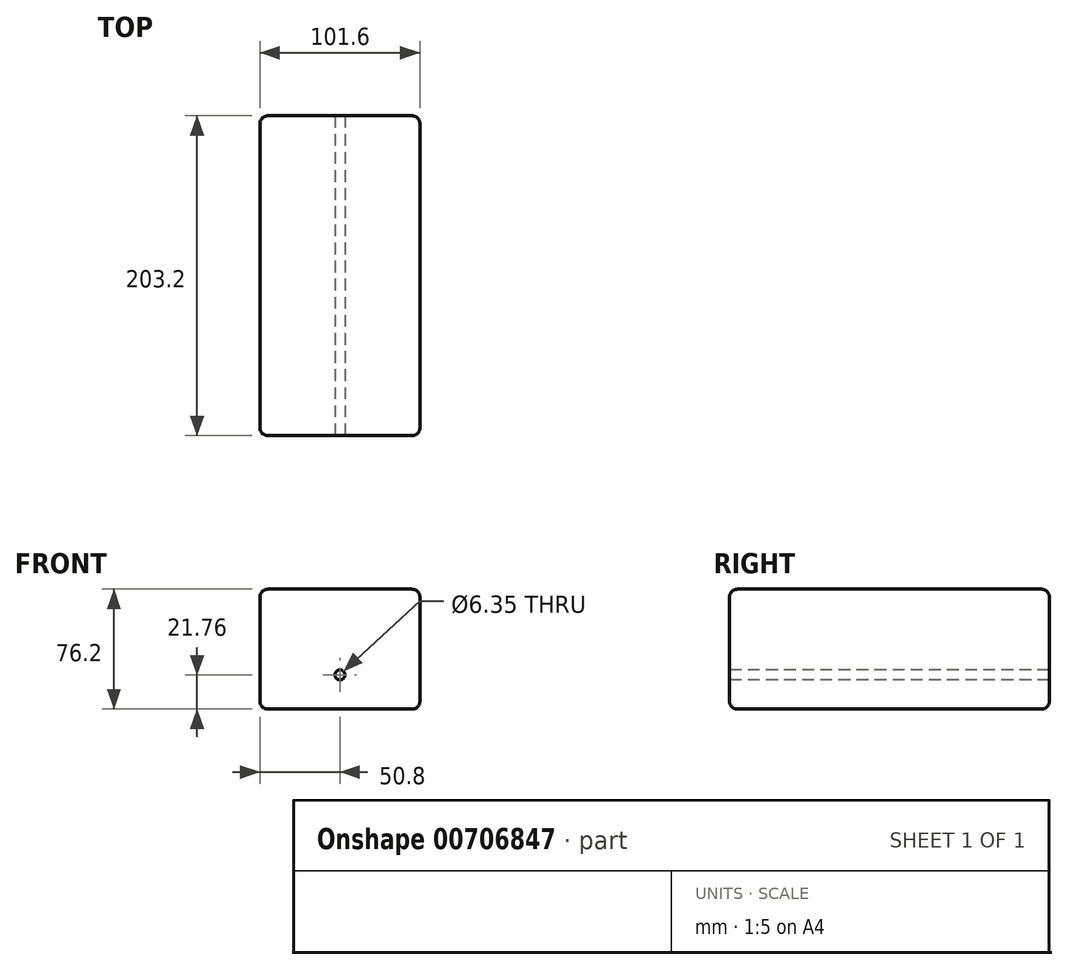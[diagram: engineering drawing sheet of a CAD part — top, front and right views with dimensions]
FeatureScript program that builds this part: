
annotation { "Feature Type Name" : "Feature", "Feature Type Description" : "" }
export const myFeature = defineFeature(function(context is Context, id is Id, definition is map)
    precondition{}
    {
        {
            var Q0;
            Q0=qCreatedBy(makeId("Front.planeOp"),FACE);
            var sketch = newSketch(context, id + "F0", { "sketchPlane" : qUnion([Q0])});
            skLineSegment(sketch, "E0.bottom", {"start": v(-50.8, -38.1) * mm, "end": v(50.8, -38.1) * mm});
            skLineSegment(sketch, "E0.top", {"start": v(-50.8, 38.1) * mm, "end": v(50.8, 38.1) * mm});
            skLineSegment(sketch, "E0.left", {"start": v(-50.8, -38.1) * mm, "end": v(-50.8, 38.1) * mm});
            skLineSegment(sketch, "E0.right", {"start": v(50.8, -38.1) * mm, "end": v(50.8, 38.1) * mm});
            skPoint(sketch, "E0.middle", {"position": v(0, 0) * mm});
            skSolve(sketch);
        }
        {
            var Q0;
            Q0=qSketchRegion(id+"F0",true);
            extrude(context, id + "F1", {"entities" : qUnion([Q0]), "endBound" : BoundingType.SYMMETRIC, "depth" : 203.2 * mm, "offsetDistance" : 25.4 * mm});
        }
        {
            var Q0;
            Q0=makeQuery(id+"F1.opExtrude","CAP_EDGE",EDGE,{"disambiguationData":[OSD([sQuery(id+"F0.wireOp",EDGE,"E0.top")])],"isStart":false});
            var Q1;
            Q1=makeQuery(id+"F1.opExtrude","SWEPT_EDGE",EDGE,{"disambiguationData":[OSD([sQuery(id+"F0.wireOp",EDGE,"E0.top"),sQuery(id+"F0.wireOp",EDGE,"E0.right")])]});
            var Q2;
            Q2=makeQuery(id+"F1.opExtrude","SWEPT_EDGE",EDGE,{"disambiguationData":[OSD([sQuery(id+"F0.wireOp",EDGE,"E0.top"),sQuery(id+"F0.wireOp",EDGE,"E0.left")])]});
            var Q3;
            Q3=makeQuery(id+"F1.opExtrude","CAP_EDGE",EDGE,{"disambiguationData":[OSD([sQuery(id+"F0.wireOp",EDGE,"E0.left")])],"isStart":false});
            var Q4;
            Q4=makeQuery(id+"F1.opExtrude","CAP_EDGE",EDGE,{"disambiguationData":[OSD([sQuery(id+"F0.wireOp",EDGE,"E0.right")])],"isStart":false});
            var Q5;
            Q5=makeQuery(id+"F1.opExtrude","CAP_FACE",FACE,{"disambiguationData":[OSD([sQuery(id+"F0.wireOp",EDGE,"E0.bottom"),sQuery(id+"F0.wireOp",EDGE,"E0.top"),sQuery(id+"F0.wireOp",EDGE,"E0.left"),sQuery(id+"F0.wireOp",EDGE,"E0.right")])],"isStart":true});
            var Q6;
            Q6=makeQuery(id+"F1.opExtrude","SWEPT_FACE",FACE,{"disambiguationData":[OSD([sQuery(id+"F0.wireOp",EDGE,"E0.right")])]});
            var Q7;
            Q7=makeQuery(id+"F1.opExtrude","SWEPT_EDGE",EDGE,{"disambiguationData":[OSD([sQuery(id+"F0.wireOp",EDGE,"E0.bottom"),sQuery(id+"F0.wireOp",EDGE,"E0.right")])]});
            var Q8;
            Q8=makeQuery(id+"F1.opExtrude","SWEPT_EDGE",EDGE,{"disambiguationData":[OSD([sQuery(id+"F0.wireOp",EDGE,"E0.bottom"),sQuery(id+"F0.wireOp",EDGE,"E0.left")])]});
            fillet(context, id + "F2", {"entities" : qUnion([Q0, Q1, Q2, Q3, Q4, Q5, Q6, Q7, Q8]), "radius" : 5.08 * mm, "tangentPropagation" : true, "allowEdgeOverflow" : false});
        }
        {
            var Q0;
            Q0=makeQuery(id+"FGfTKkmkADLqAxq_1.opShell","OFFSET_EDGE",EDGE,{"disambiguationData":[OSD([sQuery(id+"F0.wireOp",EDGE,"E0.top"),sQuery(id+"F0.wireOp",EDGE,"E0.right")])]});
            var Q1;
            {var subQ0=sQuery(id+"F0.wireOp",EDGE,"E0.top");var subQ1=makeQuery(id+"F1.opExtrude","CAP_EDGE",EDGE,{"disambiguationData":[OSD([subQ0])],"isStart":true});var subQ2=sQuery(id+"F0.wireOp",EDGE,"E0.right");var subQ3=sQuery(id+"F0.wireOp",EDGE,"E0.left");var subQ4=sQuery(id+"F0.wireOp",EDGE,"E0.bottom");Q1=makeQuery(id+"FGfTKkmkADLqAxq_1.opShell","OFFSET_EDGE",EDGE,{"disambiguationData":[OSD([subQ4,subQ0,subQ3,subQ2]),TDD([makeQuery(id+"F2.opFillet","BLEND_EDGE",EDGE,{"blendedFrom":[subQ1,makeQuery(id+"F1.opExtrude","CAP_FACE",FACE,{"disambiguationData":[OSD([subQ4,subQ0,subQ3,subQ2])],"isStart":true})],"blendedInto":[makeQuery(id+"F1.opExtrude","CAP_FACE",FACE,{"disambiguationData":[OSD([subQ4,subQ0,subQ3,subQ2])],"isStart":true})]}),makeQuery(id+"F2.opFillet","BLEND_EDGE",EDGE,{"blendedFrom":[subQ1,makeQuery(id+"F1.opExtrude","SWEPT_FACE",FACE,{"disambiguationData":[OSD([subQ0])]})],"blendedInto":[makeQuery(id+"F1.opExtrude","SWEPT_FACE",FACE,{"disambiguationData":[OSD([subQ0])]})]})])]});}
            var Q2;
            {var subQ0=sQuery(id+"F0.wireOp",EDGE,"E0.left");var subQ1=makeQuery(id+"F1.opExtrude","CAP_EDGE",EDGE,{"disambiguationData":[OSD([subQ0])],"isStart":true});var subQ2=sQuery(id+"F0.wireOp",EDGE,"E0.right");var subQ3=sQuery(id+"F0.wireOp",EDGE,"E0.top");var subQ4=sQuery(id+"F0.wireOp",EDGE,"E0.bottom");Q2=makeQuery(id+"FGfTKkmkADLqAxq_1.opShell","OFFSET_EDGE",EDGE,{"disambiguationData":[OSD([subQ4,subQ3,subQ0,subQ2]),TDD([makeQuery(id+"F2.opFillet","BLEND_EDGE",EDGE,{"blendedFrom":[subQ1,makeQuery(id+"F1.opExtrude","CAP_FACE",FACE,{"disambiguationData":[OSD([subQ4,subQ3,subQ0,subQ2])],"isStart":true})],"blendedInto":[makeQuery(id+"F1.opExtrude","CAP_FACE",FACE,{"disambiguationData":[OSD([subQ4,subQ3,subQ0,subQ2])],"isStart":true})]}),makeQuery(id+"F2.opFillet","BLEND_EDGE",EDGE,{"blendedFrom":[subQ1,makeQuery(id+"F1.opExtrude","SWEPT_FACE",FACE,{"disambiguationData":[OSD([subQ0])]})],"blendedInto":[makeQuery(id+"F1.opExtrude","SWEPT_FACE",FACE,{"disambiguationData":[OSD([subQ0])]})]})])]});}
            var Q3;
            {var subQ0=sQuery(id+"F0.wireOp",EDGE,"E0.right");var subQ1=makeQuery(id+"F1.opExtrude","CAP_EDGE",EDGE,{"disambiguationData":[OSD([subQ0])],"isStart":true});var subQ2=sQuery(id+"F0.wireOp",EDGE,"E0.left");var subQ3=sQuery(id+"F0.wireOp",EDGE,"E0.top");var subQ4=sQuery(id+"F0.wireOp",EDGE,"E0.bottom");Q3=makeQuery(id+"FGfTKkmkADLqAxq_1.opShell","OFFSET_EDGE",EDGE,{"disambiguationData":[OSD([subQ4,subQ3,subQ2,subQ0]),TDD([makeQuery(id+"F2.opFillet","BLEND_EDGE",EDGE,{"blendedFrom":[subQ1,makeQuery(id+"F1.opExtrude","CAP_FACE",FACE,{"disambiguationData":[OSD([subQ4,subQ3,subQ2,subQ0])],"isStart":true})],"blendedInto":[makeQuery(id+"F1.opExtrude","CAP_FACE",FACE,{"disambiguationData":[OSD([subQ4,subQ3,subQ2,subQ0])],"isStart":true})]}),makeQuery(id+"F2.opFillet","BLEND_EDGE",EDGE,{"blendedFrom":[subQ1,makeQuery(id+"F1.opExtrude","SWEPT_FACE",FACE,{"disambiguationData":[OSD([subQ0])]})],"blendedInto":[makeQuery(id+"F1.opExtrude","SWEPT_FACE",FACE,{"disambiguationData":[OSD([subQ0])]})]})])]});}
            var Q4;
            Q4=makeQuery(id+"FGfTKkmkADLqAxq_1.opShell","OFFSET_EDGE",EDGE,{"disambiguationData":[OSD([sQuery(id+"F0.wireOp",EDGE,"E0.top"),sQuery(id+"F0.wireOp",EDGE,"E0.left")])]});
            var Q5;
            {var subQ0=sQuery(id+"F0.wireOp",EDGE,"E0.right");var subQ1=sQuery(id+"F0.wireOp",EDGE,"E0.left");var subQ2=sQuery(id+"F0.wireOp",EDGE,"E0.top");var subQ3=sQuery(id+"F0.wireOp",EDGE,"E0.bottom");var subQ4=makeQuery(id+"F1.opExtrude","CAP_EDGE",EDGE,{"disambiguationData":[OSD([subQ3])],"isStart":true});Q5=makeQuery(id+"FGfTKkmkADLqAxq_1.opShell","OFFSET_EDGE",EDGE,{"disambiguationData":[OSD([subQ3,subQ2,subQ1,subQ0]),TDD([makeQuery(id+"F2.opFillet","BLEND_EDGE",EDGE,{"blendedFrom":[subQ4,makeQuery(id+"F1.opExtrude","SWEPT_FACE",FACE,{"disambiguationData":[OSD([subQ3])]})],"blendedInto":[makeQuery(id+"F1.opExtrude","SWEPT_FACE",FACE,{"disambiguationData":[OSD([subQ3])]})]}),makeQuery(id+"F2.opFillet","BLEND_EDGE",EDGE,{"blendedFrom":[subQ4,makeQuery(id+"F1.opExtrude","CAP_FACE",FACE,{"disambiguationData":[OSD([subQ3,subQ2,subQ1,subQ0])],"isStart":true})],"blendedInto":[makeQuery(id+"F1.opExtrude","CAP_FACE",FACE,{"disambiguationData":[OSD([subQ3,subQ2,subQ1,subQ0])],"isStart":true})]})])]});}
            var Q6;
            Q6=makeQuery(id+"FGfTKkmkADLqAxq_1.opShell","OFFSET_EDGE",EDGE,{"disambiguationData":[OSD([sQuery(id+"F0.wireOp",EDGE,"E0.bottom"),sQuery(id+"F0.wireOp",EDGE,"E0.left")])]});
            var Q7;
            Q7=makeQuery(id+"FGfTKkmkADLqAxq_1.opShell","OFFSET_EDGE",EDGE,{"disambiguationData":[OSD([sQuery(id+"F0.wireOp",EDGE,"E0.bottom")])]});
            var Q8;
            {var subQ0=sQuery(id+"F0.wireOp",EDGE,"E0.left");var subQ1=makeQuery(id+"F1.opExtrude","CAP_EDGE",EDGE,{"disambiguationData":[OSD([subQ0])],"isStart":false});var subQ2=sQuery(id+"F0.wireOp",EDGE,"E0.right");var subQ3=sQuery(id+"F0.wireOp",EDGE,"E0.top");var subQ4=sQuery(id+"F0.wireOp",EDGE,"E0.bottom");Q8=makeQuery(id+"FGfTKkmkADLqAxq_1.opShell","OFFSET_EDGE",EDGE,{"disambiguationData":[OSD([subQ4,subQ3,subQ0,subQ2]),TDD([makeQuery(id+"F2.opFillet","BLEND_EDGE",EDGE,{"blendedFrom":[subQ1,makeQuery(id+"F1.opExtrude","CAP_FACE",FACE,{"disambiguationData":[OSD([subQ4,subQ3,subQ0,subQ2])],"isStart":false})],"blendedInto":[makeQuery(id+"F1.opExtrude","CAP_FACE",FACE,{"disambiguationData":[OSD([subQ4,subQ3,subQ0,subQ2])],"isStart":false})]}),makeQuery(id+"F2.opFillet","BLEND_EDGE",EDGE,{"blendedFrom":[subQ1,makeQuery(id+"F1.opExtrude","SWEPT_FACE",FACE,{"disambiguationData":[OSD([subQ0])]})],"blendedInto":[makeQuery(id+"F1.opExtrude","SWEPT_FACE",FACE,{"disambiguationData":[OSD([subQ0])]})]})])]});}
            var Q9;
            {var subQ0=sQuery(id+"F0.wireOp",EDGE,"E0.top");var subQ1=makeQuery(id+"F1.opExtrude","CAP_EDGE",EDGE,{"disambiguationData":[OSD([subQ0])],"isStart":false});var subQ2=sQuery(id+"F0.wireOp",EDGE,"E0.right");var subQ3=sQuery(id+"F0.wireOp",EDGE,"E0.left");var subQ4=sQuery(id+"F0.wireOp",EDGE,"E0.bottom");Q9=makeQuery(id+"FGfTKkmkADLqAxq_1.opShell","OFFSET_EDGE",EDGE,{"disambiguationData":[OSD([subQ4,subQ0,subQ3,subQ2]),TDD([makeQuery(id+"F2.opFillet","BLEND_EDGE",EDGE,{"blendedFrom":[subQ1,makeQuery(id+"F1.opExtrude","CAP_FACE",FACE,{"disambiguationData":[OSD([subQ4,subQ0,subQ3,subQ2])],"isStart":false})],"blendedInto":[makeQuery(id+"F1.opExtrude","CAP_FACE",FACE,{"disambiguationData":[OSD([subQ4,subQ0,subQ3,subQ2])],"isStart":false})]}),makeQuery(id+"F2.opFillet","BLEND_EDGE",EDGE,{"blendedFrom":[subQ1,makeQuery(id+"F1.opExtrude","SWEPT_FACE",FACE,{"disambiguationData":[OSD([subQ0])]})],"blendedInto":[makeQuery(id+"F1.opExtrude","SWEPT_FACE",FACE,{"disambiguationData":[OSD([subQ0])]})]})])]});}
            var Q10;
            Q10=makeQuery(id+"FGfTKkmkADLqAxq_1.opShell","OFFSET_EDGE",EDGE,{"disambiguationData":[OSD([sQuery(id+"F0.wireOp",EDGE,"E0.bottom"),sQuery(id+"F0.wireOp",EDGE,"E0.right")])]});
            var Q11;
            {var subQ0=sQuery(id+"F0.wireOp",EDGE,"E0.right");var subQ1=makeQuery(id+"F1.opExtrude","CAP_EDGE",EDGE,{"disambiguationData":[OSD([subQ0])],"isStart":false});var subQ2=sQuery(id+"F0.wireOp",EDGE,"E0.left");var subQ3=sQuery(id+"F0.wireOp",EDGE,"E0.top");var subQ4=sQuery(id+"F0.wireOp",EDGE,"E0.bottom");Q11=makeQuery(id+"FGfTKkmkADLqAxq_1.opShell","OFFSET_EDGE",EDGE,{"disambiguationData":[OSD([subQ4,subQ3,subQ2,subQ0]),TDD([makeQuery(id+"F2.opFillet","BLEND_EDGE",EDGE,{"blendedFrom":[subQ1,makeQuery(id+"F1.opExtrude","CAP_FACE",FACE,{"disambiguationData":[OSD([subQ4,subQ3,subQ2,subQ0])],"isStart":false})],"blendedInto":[makeQuery(id+"F1.opExtrude","CAP_FACE",FACE,{"disambiguationData":[OSD([subQ4,subQ3,subQ2,subQ0])],"isStart":false})]}),makeQuery(id+"F2.opFillet","BLEND_EDGE",EDGE,{"blendedFrom":[subQ1,makeQuery(id+"F1.opExtrude","SWEPT_FACE",FACE,{"disambiguationData":[OSD([subQ0])]})],"blendedInto":[makeQuery(id+"F1.opExtrude","SWEPT_FACE",FACE,{"disambiguationData":[OSD([subQ0])]})]})])]});}
            var Q12;
            {var subQ0=sQuery(id+"F0.wireOp",EDGE,"E0.right");Q12=makeQuery(id+"F2.opFillet","BLEND_EDGE",EDGE,{"blendedFrom":[makeQuery(id+"F1.opExtrude","CAP_EDGE",EDGE,{"disambiguationData":[OSD([subQ0])],"isStart":false}),makeQuery(id+"F1.opExtrude","CAP_FACE",FACE,{"disambiguationData":[OSD([sQuery(id+"F0.wireOp",EDGE,"E0.bottom"),sQuery(id+"F0.wireOp",EDGE,"E0.top"),sQuery(id+"F0.wireOp",EDGE,"E0.left"),subQ0])],"isStart":false})],"blendedInto":[makeQuery(id+"F1.opExtrude","CAP_FACE",FACE,{"disambiguationData":[OSD([sQuery(id+"F0.wireOp",EDGE,"E0.bottom"),sQuery(id+"F0.wireOp",EDGE,"E0.top"),sQuery(id+"F0.wireOp",EDGE,"E0.left"),subQ0])],"isStart":false})]});}
            var Q13;
            {var subQ0=sQuery(id+"F0.wireOp",EDGE,"E0.bottom");Q13=makeQuery(id+"F2.opFillet","BLEND_EDGE",EDGE,{"blendedFrom":[makeQuery(id+"F1.opExtrude","SWEPT_EDGE",EDGE,{"disambiguationData":[OSD([subQ0,sQuery(id+"F0.wireOp",EDGE,"E0.right")])]}),makeQuery(id+"F1.opExtrude","SWEPT_FACE",FACE,{"disambiguationData":[OSD([subQ0])]})],"blendedInto":[makeQuery(id+"F1.opExtrude","SWEPT_FACE",FACE,{"disambiguationData":[OSD([subQ0])]})]});}
            var Q14;
            Q14=makeQuery(id+"F1.opExtrude","CAP_EDGE",EDGE,{"disambiguationData":[OSD([sQuery(id+"F0.wireOp",EDGE,"E0.bottom")])],"isStart":false});
            fillet(context, id + "F3", {"entities" : qUnion([Q0, Q1, Q2, Q3, Q4, Q5, Q6, Q7, Q8, Q9, Q10, Q11, Q12, Q13, Q14]), "radius" : 5.08 * mm, "tangentPropagation" : true, "allowEdgeOverflow" : false});
        }
        {
            var Q0;
            Q0=makeQuery(id+"F1.opExtrude","CAP_FACE",FACE,{"disambiguationData":[OSD([sQuery(id+"F0.wireOp",EDGE,"E0.bottom"),sQuery(id+"F0.wireOp",EDGE,"E0.top"),sQuery(id+"F0.wireOp",EDGE,"E0.left"),sQuery(id+"F0.wireOp",EDGE,"E0.right")])],"isStart":false});
            var sketch = newSketch(context, id + "F4", { "sketchPlane" : qUnion([Q0])});
            skCircle(sketch, "E1", {"center": v(0, -16.34) * mm, "radius": 3.18 * mm});
            skSolve(sketch);
        }
        {
            var Q0;
            Q0=makeQuery(id+"F4.imprint","IMPRINT",FACE,{"disambiguationData":[TD([[makeQuery(id+"F4.imprint","IMPRINT",EDGE,{"derivedFrom":sQuery(id+"F4.wireOp",EDGE,"E1")}),1.0]])]});
            var Q1;
            Q1=makeQuery(id+"F1.opExtrude","CAP_FACE",FACE,{"disambiguationData":[OSD([sQuery(id+"F0.wireOp",EDGE,"E0.bottom"),sQuery(id+"F0.wireOp",EDGE,"E0.top"),sQuery(id+"F0.wireOp",EDGE,"E0.left"),sQuery(id+"F0.wireOp",EDGE,"E0.right")])],"isStart":true});
            extrude(context, id + "F5", {"entities" : qUnion([Q0]), "operationType" : NewBodyOperationType.REMOVE, "endBound" : BoundingType.UP_TO_SURFACE, "oppositeDirection" : true, "depth" : 63.5 * mm, "endBoundEntityFace" : qUnion([Q1]), "offsetDistance" : 25.4 * mm});
        }
        {
            var Q0;
            Q0=makeQuery(id+"F1.opExtrude","CAP_FACE",FACE,{"disambiguationData":[OSD([sQuery(id+"F0.wireOp",EDGE,"E0.bottom"),sQuery(id+"F0.wireOp",EDGE,"E0.top"),sQuery(id+"F0.wireOp",EDGE,"E0.left"),sQuery(id+"F0.wireOp",EDGE,"E0.right")])],"isStart":false});
            var sketch = newSketch(context, id + "F6", { "sketchPlane" : qUnion([Q0])});
            skCircle(sketch, "E2", {"center": v(0, -16.34) * mm, "radius": 3.17 * mm});
            skSolve(sketch);
        }
        {
            var Q0;
            Q0=qSketchRegion(id+"F6",true);
            var Q1;
            Q1=sQuery(id+"F6.wireOp",EDGE,"E2");
            extrude(context, id + "F7", {"entities" : qUnion([Q0]), "bodyType" : ToolBodyType.SURFACE, "surfaceEntities" : qUnion([Q1]), "depth" : 127 * mm, "offsetDistance" : 25.4 * mm});
        }
        {
            var Q0;
            Q0=makeQuery(id+"F1.opExtrude","CAP_FACE",FACE,{"disambiguationData":[OSD([sQuery(id+"F0.wireOp",EDGE,"E0.bottom"),sQuery(id+"F0.wireOp",EDGE,"E0.top"),sQuery(id+"F0.wireOp",EDGE,"E0.left"),sQuery(id+"F0.wireOp",EDGE,"E0.right")])],"isStart":true});
            var sketch = newSketch(context, id + "F8", { "sketchPlane" : qUnion([Q0])});
            skCircle(sketch, "E3", {"center": v(0, -16.34) * mm, "radius": 3.18 * mm});
            skSolve(sketch);
        }
        {
            var Q0;
            Q0=qSketchRegion(id+"F8",true);
            var Q1;
            Q1=qConstructionFilter(qBodyType(qCreatedBy(id+"F8",EDGE),BodyType.WIRE),ConstructionObject.NO);
            extrude(context, id + "F9", {"entities" : qUnion([Q0]), "bodyType" : ToolBodyType.SURFACE, "operationType" : NewBodyOperationType.ADD, "surfaceEntities" : qUnion([Q1]), "depth" : 127 * mm, "hasOffset" : true, "offsetDistance" : 127 * mm});
        }
    });
